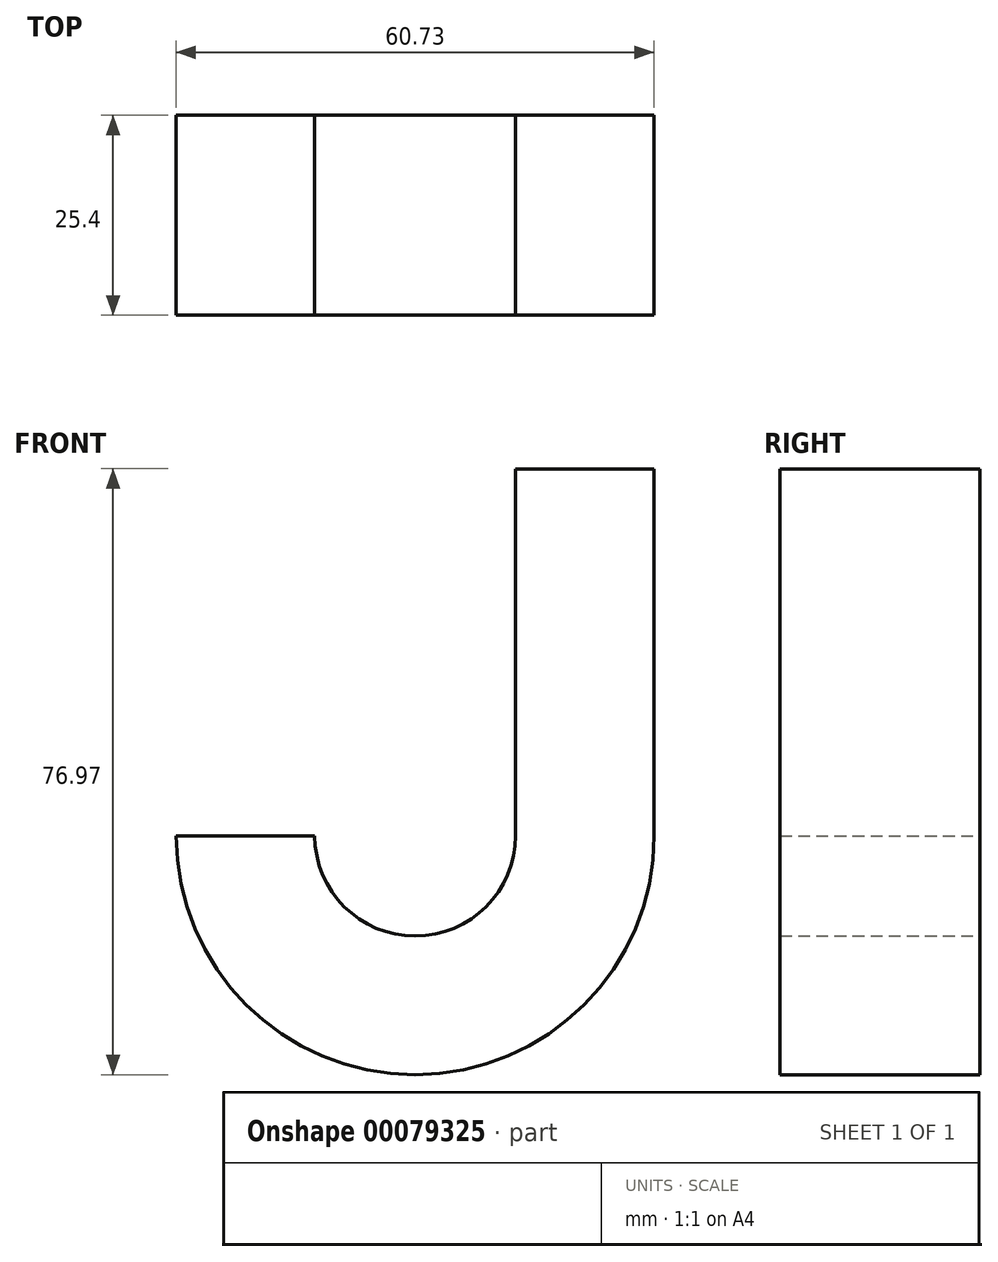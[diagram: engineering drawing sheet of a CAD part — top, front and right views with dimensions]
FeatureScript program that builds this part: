
annotation { "Feature Type Name" : "Feature", "Feature Type Description" : "" }
export const myFeature = defineFeature(function(context is Context, id is Id, definition is map)
    precondition{}
    {
        {
            var Q0;
            Q0=qCreatedBy(makeId("Front.planeOp"),FACE);
            var sketch = newSketch(context, id + "F0", { "sketchPlane" : qUnion([Q0])});
            skLineSegment(sketch, "E0.bottom", {"start": v(0, 46.6) * mm, "end": v(17.61, 46.6) * mm});
            skLineSegment(sketch, "E0.top", {"start": v(0, 0) * mm, "end": v(17.61, 0) * mm});
            skLineSegment(sketch, "E0.left", {"start": v(0, 46.6) * mm, "end": v(0, 0) * mm});
            skLineSegment(sketch, "E0.right", {"start": v(17.61, 46.6) * mm, "end": v(17.61, 0) * mm});
            skArc(sketch, "E1", {"start": v(-25.5, 0) * mm, "mid": v(-12.75, -12.75) * mm, "end": v(0, 0) * mm});
            skArc(sketch, "E2", {"start": v(-43.12, 0) * mm, "mid": v(-12.75, -30.36) * mm, "end": v(17.61, 0) * mm});
            skLineSegment(sketch, "E3", {"start": v(-43.12, 0) * mm, "end": v(-25.5, 0) * mm});
            skSolve(sketch);
        }
        {
            var Q0;
            Q0 = qSketchRegion(id + "F0", true);
            extrude(context, id + "F1", {"entities" : qUnion([Q0]), "depth" : 25.4 * mm});
        }
    });
